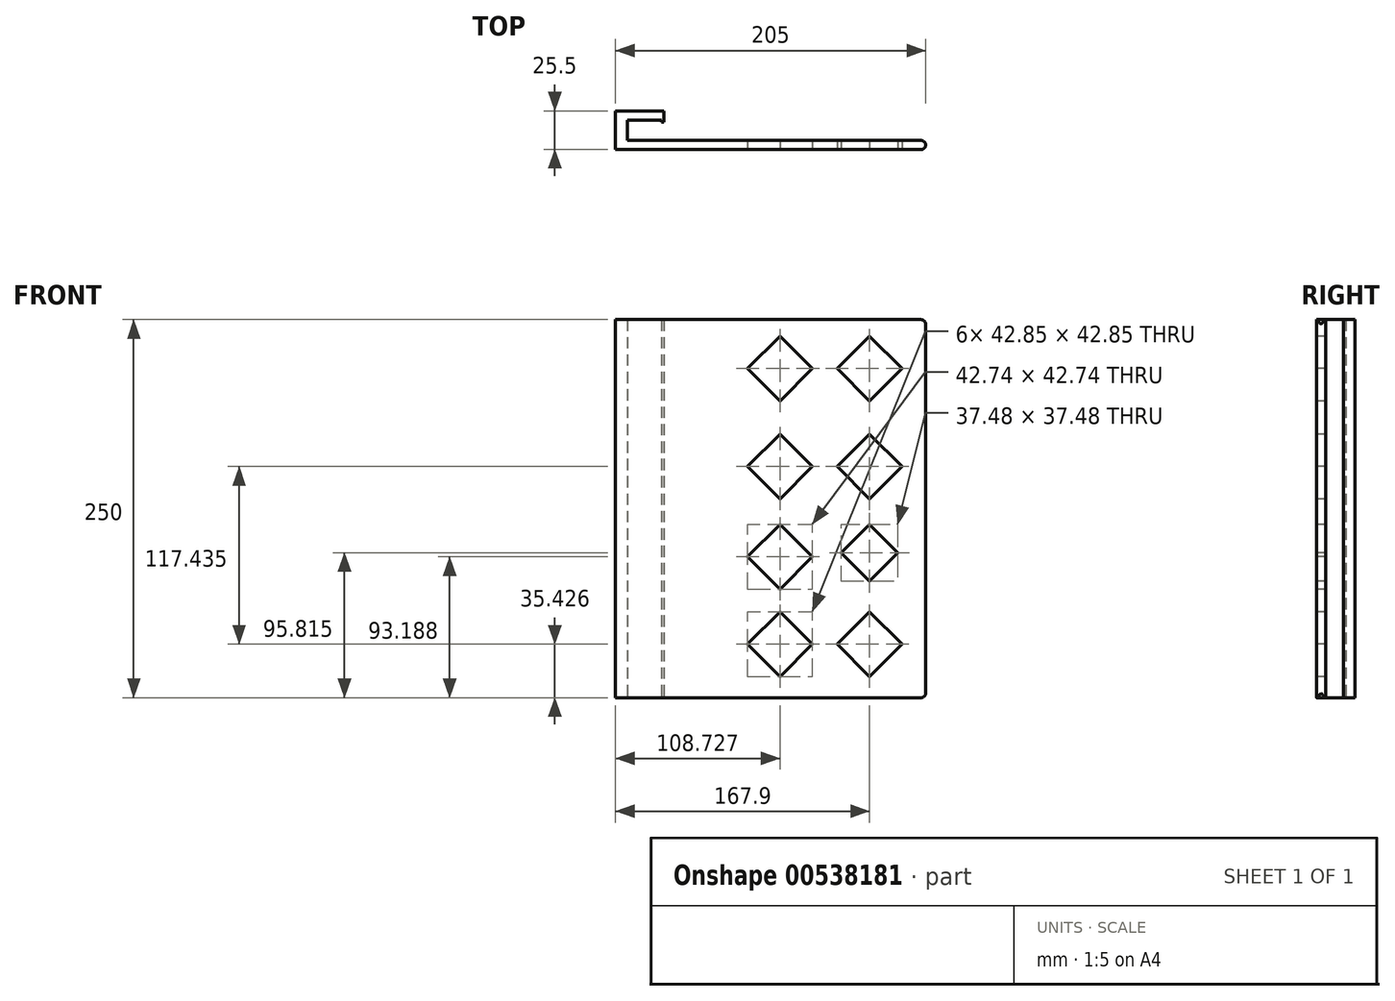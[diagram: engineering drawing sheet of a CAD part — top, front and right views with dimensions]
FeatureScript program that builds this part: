
annotation { "Feature Type Name" : "Feature", "Feature Type Description" : "" }
export const myFeature = defineFeature(function(context is Context, id is Id, definition is map)
    precondition{}
    {
        {
            var Q0;
            Q0=qCreatedBy(makeId("Top.planeOp"),FACE);
            var sketch = newSketch(context, id + "F0", { "sketchPlane" : qUnion([Q0])});
            skLineSegment(sketch, "E0.bottom", {"start": v(0, 0) * mm, "end": v(205, 0) * mm});
            skLineSegment(sketch, "E0.top", {"start": v(0, 6) * mm, "end": v(205, 6) * mm});
            skLineSegment(sketch, "E0.left", {"start": v(0, 0) * mm, "end": v(0, 6) * mm});
            skLineSegment(sketch, "E0.right", {"start": v(205, 0) * mm, "end": v(205, 6) * mm});
            skLineSegment(sketch, "E1.bottom", {"start": v(0, 0) * mm, "end": v(7.95, 0) * mm});
            skLineSegment(sketch, "E1.top", {"start": v(0, 25.5) * mm, "end": v(7.95, 25.5) * mm});
            skLineSegment(sketch, "E1.left", {"start": v(0, 0) * mm, "end": v(0, 25.5) * mm});
            skLineSegment(sketch, "E1.right", {"start": v(7.95, 0) * mm, "end": v(7.95, 25.5) * mm});
            skLineSegment(sketch, "E2.bottom", {"start": v(0, 25.5) * mm, "end": v(32, 25.5) * mm});
            skLineSegment(sketch, "E2.top", {"start": v(0, 19.5) * mm, "end": v(32, 19.5) * mm});
            skLineSegment(sketch, "E2.left", {"start": v(0, 25.5) * mm, "end": v(0, 19.5) * mm});
            skLineSegment(sketch, "E2.right", {"start": v(32, 25.5) * mm, "end": v(32, 19.5) * mm});
            skLineSegment(sketch, "E3.bottom", {"start": v(32, 19.5) * mm, "end": v(30.5, 19.5) * mm});
            skLineSegment(sketch, "E3.top", {"start": v(32, 18) * mm, "end": v(30.5, 18) * mm});
            skLineSegment(sketch, "E3.left", {"start": v(32, 19.5) * mm, "end": v(32, 18) * mm});
            skLineSegment(sketch, "E3.right", {"start": v(30.5, 19.5) * mm, "end": v(30.5, 18) * mm});
            skSolve(sketch);
        }
        {
            var Q0;
            {var subQ0=sQuery(id+"F0.wireOp",EDGE,"E0.bottom");Q0=makeQuery(id+"F0.imprint","IMPRINT",FACE,{"disambiguationData":[TD([[makeQuery(id+"F0.imprint","IMPRINT",EDGE,{"derivedFrom":subQ0}),1.0]])]});}
            var Q1;
            {var subQ0=sQuery(id+"F0.wireOp",EDGE,"E1.left");var subQ1=sQuery(id+"F0.wireOp",EDGE,"E0.top");var subQ2=makeQuery(id+"F0.imprint","INTERSECT",VERTEX,{"derivedFrom":[subQ1,subQ0]});Q1=makeQuery(id+"F0.imprint","IMPRINT",FACE,{"disambiguationData":[TD([[makeQuery(id+"F0.imprint","IMPRINT",EDGE,{"disambiguationData":[TD([[subQ2,-1.0]])],"derivedFrom":subQ1}),1.0]])]});}
            var Q2;
            Q2 = qSketchRegion(id + "F0", true);
            var Q3;
            {var subQ5=sQuery(id+"F0.wireOp",EDGE,"E2.left");Q3=makeQuery(id+"F0.imprint","IMPRINT",FACE,{"disambiguationData":[TD([[makeQuery(id+"F0.imprint","IMPRINT",EDGE,{"derivedFrom":subQ5}),1.0]])]});}
            var Q4;
            {var subQ5=sQuery(id+"F0.wireOp",EDGE,"E2.right");Q4=makeQuery(id+"F0.imprint","IMPRINT",FACE,{"disambiguationData":[TD([[makeQuery(id+"F0.imprint","IMPRINT",EDGE,{"derivedFrom":subQ5}),-1.0]])]});}
            var Q5;
            {var subQ5=sQuery(id+"F0.wireOp",EDGE,"E1.bottom");Q5=makeQuery(id+"F0.imprint","IMPRINT",FACE,{"disambiguationData":[TD([[makeQuery(id+"F0.imprint","IMPRINT",EDGE,{"derivedFrom":subQ5}),1.0]])]});}
            extrude(context, id + "F1", {"entities" : qUnion([Q0, Q1, Q2, Q3, Q4, Q5]), "depth" : 250 * mm, "offsetDistance" : 25 * mm});
        }
        {
            var Q0;
            Q0=makeQuery(id+"F1.opExtrude","SWEPT_FACE",FACE,{"disambiguationData":[OSD([sQuery(id+"F0.wireOp",EDGE,"E0.bottom"),sQuery(id+"F0.wireOp",EDGE,"E1.bottom")])]});
            var sketch = newSketch(context, id + "F2", { "sketchPlane" : qUnion([Q0])});
            skLineSegment(sketch, "E4", {"start": v(244.61, 15.89) * mm, "end": v(266.04, 37.31) * mm});
            skLineSegment(sketch, "E5", {"start": v(266.04, 37.31) * mm, "end": v(244.61, 58.74) * mm});
            skLineSegment(sketch, "E6", {"start": v(244.61, 15.89) * mm, "end": v(223.19, 37.31) * mm});
            skLineSegment(sketch, "E7", {"start": v(223.19, 37.31) * mm, "end": v(244.61, 58.74) * mm});
            skLineSegment(sketch, "E8", {"start": v(167.9, 14) * mm, "end": v(189.33, 35.43) * mm});
            skLineSegment(sketch, "E9", {"start": v(189.33, 35.43) * mm, "end": v(167.9, 56.85) * mm});
            skLineSegment(sketch, "E10", {"start": v(167.9, 14) * mm, "end": v(146.47, 35.43) * mm});
            skLineSegment(sketch, "E11", {"start": v(146.47, 35.43) * mm, "end": v(167.9, 56.85) * mm});
            skLineSegment(sketch, "E12", {"start": v(108.73, 14) * mm, "end": v(130.15, 35.43) * mm});
            skLineSegment(sketch, "E13", {"start": v(130.15, 35.43) * mm, "end": v(108.73, 56.85) * mm});
            skLineSegment(sketch, "E14", {"start": v(108.73, 14) * mm, "end": v(87.3, 35.43) * mm});
            skLineSegment(sketch, "E15", {"start": v(87.3, 35.43) * mm, "end": v(108.73, 56.85) * mm});
            skLineSegment(sketch, "E16", {"start": v(167.9, 77.07) * mm, "end": v(186.64, 95.82) * mm});
            skLineSegment(sketch, "E17", {"start": v(186.64, 95.82) * mm, "end": v(167.9, 114.56) * mm});
            skLineSegment(sketch, "E18", {"start": v(167.9, 77.07) * mm, "end": v(149.16, 95.82) * mm});
            skLineSegment(sketch, "E19", {"start": v(149.16, 95.82) * mm, "end": v(167.9, 114.56) * mm});
            skLineSegment(sketch, "E20", {"start": v(108.73, 71.82) * mm, "end": v(130.1, 93.19) * mm});
            skLineSegment(sketch, "E21", {"start": v(130.1, 93.19) * mm, "end": v(108.73, 114.56) * mm});
            skLineSegment(sketch, "E22", {"start": v(108.73, 71.82) * mm, "end": v(87.36, 93.19) * mm});
            skLineSegment(sketch, "E23", {"start": v(87.36, 93.19) * mm, "end": v(108.73, 114.56) * mm});
            skLineSegment(sketch, "E24", {"start": v(167.9, 131.43) * mm, "end": v(189.33, 152.86) * mm});
            skLineSegment(sketch, "E25", {"start": v(189.33, 152.86) * mm, "end": v(167.9, 174.29) * mm});
            skLineSegment(sketch, "E26", {"start": v(167.9, 131.43) * mm, "end": v(146.47, 152.86) * mm});
            skLineSegment(sketch, "E27", {"start": v(146.47, 152.86) * mm, "end": v(167.9, 174.29) * mm});
            skLineSegment(sketch, "E28", {"start": v(108.73, 131.43) * mm, "end": v(130.15, 152.86) * mm});
            skLineSegment(sketch, "E29", {"start": v(130.15, 152.86) * mm, "end": v(108.73, 174.29) * mm});
            skLineSegment(sketch, "E30", {"start": v(108.73, 131.43) * mm, "end": v(87.3, 152.86) * mm});
            skLineSegment(sketch, "E31", {"start": v(87.3, 152.86) * mm, "end": v(108.73, 174.29) * mm});
            skLineSegment(sketch, "E32", {"start": v(167.9, 196.31) * mm, "end": v(189.33, 217.74) * mm});
            skLineSegment(sketch, "E33", {"start": v(189.33, 217.74) * mm, "end": v(167.9, 239.16) * mm});
            skLineSegment(sketch, "E34", {"start": v(167.9, 196.31) * mm, "end": v(146.47, 217.74) * mm});
            skLineSegment(sketch, "E35", {"start": v(146.47, 217.74) * mm, "end": v(167.9, 239.16) * mm});
            skLineSegment(sketch, "E36", {"start": v(108.73, 196.31) * mm, "end": v(130.15, 217.74) * mm});
            skLineSegment(sketch, "E37", {"start": v(130.15, 217.74) * mm, "end": v(108.73, 239.16) * mm});
            skLineSegment(sketch, "E38", {"start": v(108.73, 196.31) * mm, "end": v(87.3, 217.74) * mm});
            skLineSegment(sketch, "E39", {"start": v(87.3, 217.74) * mm, "end": v(108.73, 239.16) * mm});
            skSolve(sketch);
        }
        {
            var Q0;
            Q0=makeQuery(id+"F2.imprint","IMPRINT",FACE,{"disambiguationData":[TD([[makeQuery(id+"F2.imprint","IMPRINT",EDGE,{"derivedFrom":sQuery(id+"F2.wireOp",EDGE,"E12")}),1.0]])]});
            var Q1;
            Q1=makeQuery(id+"F2.imprint","IMPRINT",FACE,{"disambiguationData":[TD([[makeQuery(id+"F2.imprint","IMPRINT",EDGE,{"derivedFrom":sQuery(id+"F2.wireOp",EDGE,"E8")}),1.0]])]});
            var Q2;
            Q2=makeQuery(id+"F2.imprint","IMPRINT",FACE,{"disambiguationData":[TD([[makeQuery(id+"F2.imprint","IMPRINT",EDGE,{"derivedFrom":sQuery(id+"F2.wireOp",EDGE,"E16")}),1.0]])]});
            var Q3;
            Q3=makeQuery(id+"F2.imprint","IMPRINT",FACE,{"disambiguationData":[TD([[makeQuery(id+"F2.imprint","IMPRINT",EDGE,{"derivedFrom":sQuery(id+"F2.wireOp",EDGE,"E20")}),1.0]])]});
            var Q4;
            Q4=makeQuery(id+"F2.imprint","IMPRINT",FACE,{"disambiguationData":[TD([[makeQuery(id+"F2.imprint","IMPRINT",EDGE,{"derivedFrom":sQuery(id+"F2.wireOp",EDGE,"E28")}),1.0]])]});
            var Q5;
            Q5=makeQuery(id+"F2.imprint","IMPRINT",FACE,{"disambiguationData":[TD([[makeQuery(id+"F2.imprint","IMPRINT",EDGE,{"derivedFrom":sQuery(id+"F2.wireOp",EDGE,"E24")}),1.0]])]});
            var Q6;
            Q6=makeQuery(id+"F2.imprint","IMPRINT",FACE,{"disambiguationData":[TD([[makeQuery(id+"F2.imprint","IMPRINT",EDGE,{"derivedFrom":sQuery(id+"F2.wireOp",EDGE,"E32")}),1.0]])]});
            var Q7;
            Q7=makeQuery(id+"F2.imprint","IMPRINT",FACE,{"disambiguationData":[TD([[makeQuery(id+"F2.imprint","IMPRINT",EDGE,{"derivedFrom":sQuery(id+"F2.wireOp",EDGE,"E36")}),1.0]])]});
            extrude(context, id + "F3", {"entities" : qUnion([Q0, Q1, Q2, Q3, Q4, Q5, Q6, Q7]), "operationType" : NewBodyOperationType.REMOVE, "oppositeDirection" : true, "depth" : 25 * mm, "offsetDistance" : 25 * mm});
        }
        {
            var Q0;
            Q0=makeQuery(id+"F1.opExtrude","SWEPT_FACE",FACE,{"disambiguationData":[OSD([sQuery(id+"F0.wireOp",EDGE,"E0.right")])]});
            fillet(context, id + "F4", {"entities" : qUnion([Q0]), "radius" : 3 * mm, "tangentPropagation" : true, "allowEdgeOverflow" : false});
        }
    });
